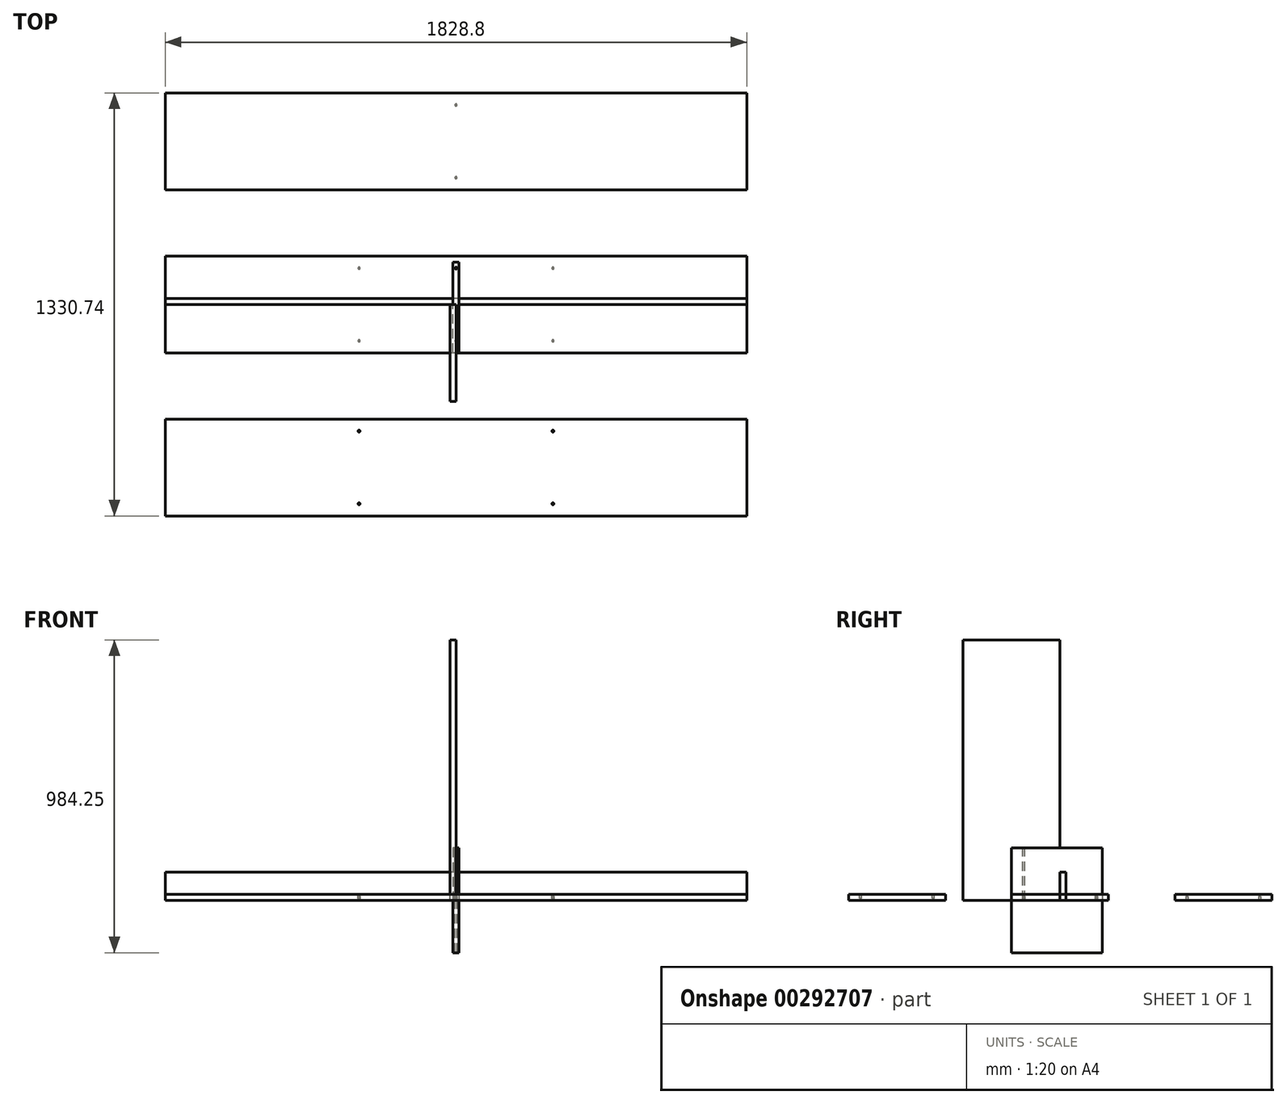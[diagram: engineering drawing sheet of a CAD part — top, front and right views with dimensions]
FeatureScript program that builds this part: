
annotation { "Feature Type Name" : "Feature", "Feature Type Description" : "" }
export const myFeature = defineFeature(function(context is Context, id is Id, definition is map)
    precondition{}
    {
        {
            var Q0;
            Q0=qCreatedBy(makeId("Top.planeOp"),FACE);
            var sketch = newSketch(context, id + "F0", { "sketchPlane" : qUnion([Q0])});
            skLineSegment(sketch, "E0.bottom", {"start": v(914.4, 152.4) * mm, "end": v(-914.4, 152.4) * mm});
            skLineSegment(sketch, "E0.top", {"start": v(914.4, -152.4) * mm, "end": v(-914.4, -152.4) * mm});
            skLineSegment(sketch, "E0.left", {"start": v(914.4, 152.4) * mm, "end": v(914.4, -152.4) * mm});
            skLineSegment(sketch, "E0.right", {"start": v(-914.4, 152.4) * mm, "end": v(-914.4, -152.4) * mm});
            skPoint(sketch, "E0.middle", {"position": v(0, 0) * mm});
            skLineSegment(sketch, "E1.bottom", {"start": v(914.4, 665.76) * mm, "end": v(-914.4, 665.76) * mm});
            skLineSegment(sketch, "E1.top", {"start": v(914.4, 360.96) * mm, "end": v(-914.4, 360.96) * mm});
            skLineSegment(sketch, "E1.left", {"start": v(914.4, 665.76) * mm, "end": v(914.4, 360.96) * mm});
            skLineSegment(sketch, "E1.right", {"start": v(-914.4, 665.76) * mm, "end": v(-914.4, 360.96) * mm});
            skPoint(sketch, "E1.middle", {"position": v(0, 513.36) * mm});
            skLineSegment(sketch, "E2.bottom", {"start": v(914.4, -360.18) * mm, "end": v(-914.4, -360.18) * mm});
            skLineSegment(sketch, "E2.top", {"start": v(914.4, -664.98) * mm, "end": v(-914.4, -664.98) * mm});
            skLineSegment(sketch, "E2.left", {"start": v(914.4, -360.18) * mm, "end": v(914.4, -664.98) * mm});
            skLineSegment(sketch, "E2.right", {"start": v(-914.4, -360.18) * mm, "end": v(-914.4, -664.98) * mm});
            skPoint(sketch, "E2.middle", {"position": v(0, -512.58) * mm});
            skSolve(sketch);
        }
        {
            var Q0;
            Q0=makeQuery(id+"F0.imprint","IMPRINT",FACE,{"disambiguationData":[TD([[makeQuery(id+"F0.imprint","IMPRINT",EDGE,{"derivedFrom":sQuery(id+"F0.wireOp",EDGE,"E2.bottom")}),1.0]])]});
            var Q1;
            Q1=makeQuery(id+"F0.imprint","IMPRINT",FACE,{"disambiguationData":[TD([[makeQuery(id+"F0.imprint","IMPRINT",EDGE,{"derivedFrom":sQuery(id+"F0.wireOp",EDGE,"E0.bottom")}),1.0]])]});
            var Q2;
            Q2=makeQuery(id+"F0.imprint","IMPRINT",FACE,{"disambiguationData":[TD([[makeQuery(id+"F0.imprint","IMPRINT",EDGE,{"derivedFrom":sQuery(id+"F0.wireOp",EDGE,"E1.bottom")}),1.0]])]});
            extrude(context, id + "F1", {"entities" : qUnion([Q0, Q1, Q2]), "depth" : 19.05 * mm});
        }
        {
            var Q0;
            Q0=makeQuery(id+"F1.opExtrude","CAP_FACE",FACE,{"disambiguationData":[OSD([sQuery(id+"F0.wireOp",EDGE,"E0.bottom"),sQuery(id+"F0.wireOp",EDGE,"E0.top"),sQuery(id+"F0.wireOp",EDGE,"E0.left"),sQuery(id+"F0.wireOp",EDGE,"E0.right")])],"isStart":false});
            var sketch = newSketch(context, id + "F2", { "sketchPlane" : qUnion([Q0])});
            skCircle(sketch, "E3", {"center": v(0, 114.3) * mm, "radius": 3.18 * mm});
            skCircle(sketch, "E4.MirrorC", {"center": v(0, -114.3) * mm, "radius": 3.18 * mm});
            skCircle(sketch, "E5", {"center": v(-304.8, -398.28) * mm, "radius": 3.18 * mm});
            skLineSegment(sketch, "E6.bottom", {"start": v(-304.8, -398.28) * mm, "end": v(304.8, -398.28) * mm, "construction": true});
            skLineSegment(sketch, "E6.top", {"start": v(-304.8, -626.88) * mm, "end": v(304.8, -626.88) * mm, "construction": true});
            skLineSegment(sketch, "E6.left", {"start": v(-304.8, -398.28) * mm, "end": v(-304.8, -626.88) * mm, "construction": true});
            skLineSegment(sketch, "E6.right", {"start": v(304.8, -398.28) * mm, "end": v(304.8, -626.88) * mm, "construction": true});
            skPoint(sketch, "E6.middle", {"position": v(0, -512.58) * mm});
            skCircle(sketch, "E7", {"center": v(-304.8, -626.88) * mm, "radius": 3.18 * mm});
            skCircle(sketch, "E8", {"center": v(304.8, -626.88) * mm, "radius": 3.18 * mm});
            skCircle(sketch, "E9", {"center": v(304.8, -398.28) * mm, "radius": 3.18 * mm});
            skLineSegment(sketch, "E10", {"start": v(-914.4, -512.58) * mm, "end": v(0, -512.58) * mm, "construction": true});
            skLineSegment(sketch, "E11", {"start": v(0, 114.3) * mm, "end": v(0, -114.3) * mm, "construction": true});
            skSolve(sketch);
        }
        {
            var Q0;
            Q0 = qSketchRegion(id + "F2", true);
            extrude(context, id + "F3", {"entities" : qUnion([Q0]), "operationType" : NewBodyOperationType.REMOVE, "oppositeDirection" : true, "depth" : 12.7 * mm});
        }
        {
            var Q0;
            Q0=qCreatedBy(makeId("Front.planeOp"),FACE);
            var sketch = newSketch(context, id + "F4", { "sketchPlane" : qUnion([Q0])});
            skLineSegment(sketch, "E12.bottom", {"start": v(0, 0) * mm, "end": v(-19.05, 0) * mm});
            skLineSegment(sketch, "E12.top", {"start": v(0, 819.15) * mm, "end": v(-19.05, 819.15) * mm});
            skLineSegment(sketch, "E12.left", {"start": v(0, 0) * mm, "end": v(0, 819.15) * mm});
            skLineSegment(sketch, "E12.right", {"start": v(-19.05, 0) * mm, "end": v(-19.05, 819.15) * mm});
            skSolve(sketch);
        }
        {
            var Q0;
            Q0 = qSketchRegion(id + "F4", true);
            extrude(context, id + "F5", {"entities" : qUnion([Q0]), "depth" : 304.8 * mm});
        }
        {
            var Q0;
            Q0=qCreatedBy(makeId("Front.planeOp"),FACE);
            var sketch = newSketch(context, id + "F6", { "sketchPlane" : qUnion([Q0])});
            skLineSegment(sketch, "E13.bottom", {"start": v(9.53, 165.1) * mm, "end": v(-9.52, 165.1) * mm});
            skLineSegment(sketch, "E13.top", {"start": v(9.53, -165.1) * mm, "end": v(-9.53, -165.1) * mm});
            skLineSegment(sketch, "E13.left", {"start": v(9.53, 165.1) * mm, "end": v(9.53, -165.1) * mm});
            skLineSegment(sketch, "E13.right", {"start": v(-9.52, 165.1) * mm, "end": v(-9.53, -165.1) * mm});
            skPoint(sketch, "E13.middle", {"position": v(0, 0) * mm});
            skSolve(sketch);
        }
        {
            var Q0;
            Q0 = qSketchRegion(id + "F6", true);
            extrude(context, id + "F7", {"entities" : qUnion([Q0]), "depth" : 152.4 * mm, "hasSecondDirection" : true, "secondDirectionOppositeDirection" : true, "secondDirectionDepth" : 133.35 * mm});
        }
        {
            var Q0;
            Q0=makeQuery(id+"F7.opExtrude","SWEPT_FACE",FACE,{"disambiguationData":[OSD([sQuery(id+"F6.wireOp",EDGE,"E13.bottom")])]});
            var sketch = newSketch(context, id + "F8", { "sketchPlane" : qUnion([Q0])});
            skCircle(sketch, "E14.0", {"center": v(0, 114.3) * mm, "radius": 3.18 * mm});
            skCircle(sketch, "E15.0", {"center": v(0, -114.3) * mm, "radius": 3.18 * mm});
            skSolve(sketch);
        }
        {
            var Q0;
            Q0 = qSketchRegion(id + "F8", true);
            extrude(context, id + "F9", {"entities" : qUnion([Q0]), "operationType" : NewBodyOperationType.REMOVE, "endBound" : BoundingType.THROUGH_ALL, "oppositeDirection" : true, "depth" : 12.7 * mm});
        }
        {
            var Q0;
            Q0=makeQuery(id+"F1.opExtrude","CAP_FACE",FACE,{"disambiguationData":[OSD([sQuery(id+"F0.wireOp",EDGE,"E0.bottom"),sQuery(id+"F0.wireOp",EDGE,"E0.top"),sQuery(id+"F0.wireOp",EDGE,"E0.left"),sQuery(id+"F0.wireOp",EDGE,"E0.right")])],"isStart":true});
            var sketch = newSketch(context, id + "F10", { "sketchPlane" : qUnion([Q0])});
            skLineSegment(sketch, "E16", {"start": v(0, -399.06) * mm, "end": v(0, -627.66) * mm, "construction": true});
            skLineSegment(sketch, "E17.bottom", {"start": v(304.8, 114.3) * mm, "end": v(-304.8, 114.3) * mm, "construction": true});
            skLineSegment(sketch, "E17.top", {"start": v(304.8, -114.3) * mm, "end": v(-304.8, -114.3) * mm, "construction": true});
            skLineSegment(sketch, "E17.left", {"start": v(304.8, 114.3) * mm, "end": v(304.8, -114.3) * mm, "construction": true});
            skLineSegment(sketch, "E17.right", {"start": v(-304.8, 114.3) * mm, "end": v(-304.8, -114.3) * mm, "construction": true});
            skPoint(sketch, "E17.middle", {"position": v(0, 0) * mm});
            skCircle(sketch, "E18", {"center": v(-304.8, 114.3) * mm, "radius": 3.18 * mm});
            skCircle(sketch, "E19", {"center": v(-304.8, -114.3) * mm, "radius": 3.18 * mm});
            skCircle(sketch, "E20", {"center": v(304.8, -114.3) * mm, "radius": 3.18 * mm});
            skCircle(sketch, "E21", {"center": v(304.8, 114.3) * mm, "radius": 3.18 * mm});
            skCircle(sketch, "E22", {"center": v(0, -399.06) * mm, "radius": 3.18 * mm});
            skCircle(sketch, "E23", {"center": v(0, -627.66) * mm, "radius": 3.18 * mm});
            skLineSegment(sketch, "E24", {"start": v(-914.4, -513.36) * mm, "end": v(0, -513.36) * mm, "construction": true});
            skSolve(sketch);
        }
        {
            var Q0;
            Q0 = qSketchRegion(id + "F10", true);
            extrude(context, id + "F11", {"entities" : qUnion([Q0]), "operationType" : NewBodyOperationType.REMOVE, "oppositeDirection" : true, "depth" : 12.7 * mm});
        }
        {
            var Q0;
            Q0=qCreatedBy(makeId("Right.planeOp"),FACE);
            var sketch = newSketch(context, id + "F12", { "sketchPlane" : qUnion([Q0])});
            skLineSegment(sketch, "E25.bottom", {"start": v(0, 0) * mm, "end": v(19.05, 0) * mm});
            skLineSegment(sketch, "E25.top", {"start": v(0, 88.9) * mm, "end": v(19.05, 88.9) * mm});
            skLineSegment(sketch, "E25.left", {"start": v(0, 0) * mm, "end": v(0, 88.9) * mm});
            skLineSegment(sketch, "E25.right", {"start": v(19.05, 0) * mm, "end": v(19.05, 88.9) * mm});
            skSolve(sketch);
        }
        {
            var Q0;
            Q0=makeQuery(id+"F12.imprint","IMPRINT",FACE,{"disambiguationData":[TD([[makeQuery(id+"F12.imprint","IMPRINT",EDGE,{"derivedFrom":sQuery(id+"F12.wireOp",EDGE,"E25.bottom")}),1.0]])]});
            extrude(context, id + "F13", {"entities" : qUnion([Q0]), "endBound" : BoundingType.SYMMETRIC, "depth" : 1828.8 * mm});
        }
    });
